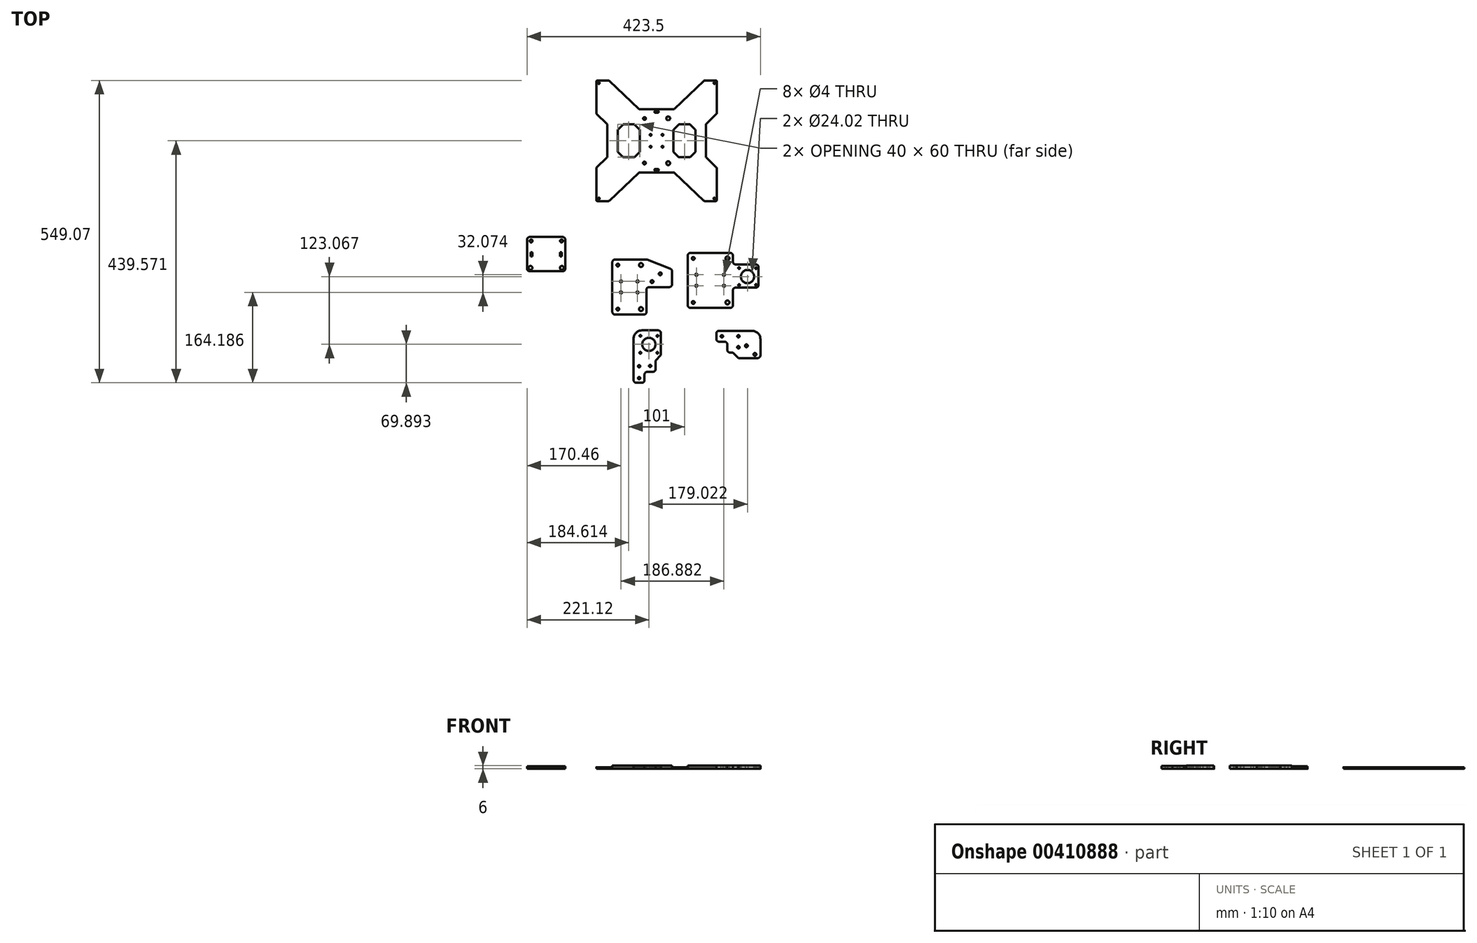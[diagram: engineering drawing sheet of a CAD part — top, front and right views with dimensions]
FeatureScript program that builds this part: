
annotation { "Feature Type Name" : "Feature", "Feature Type Description" : "" }
export const myFeature = defineFeature(function(context is Context, id is Id, definition is map)
    precondition{}
    {
        {
            var Q0;
            Q0=qCreatedBy(makeId("Top.planeOp"),FACE);
            var sketch = newSketch(context, id + "F0", { "sketchPlane" : qUnion([Q0])});
            skLineSegment(sketch, "E0", {"start": v(-27.76, 55) * mm, "end": v(-27.76, -40.26) * mm});
            skLineSegment(sketch, "E1", {"start": v(-27.76, -40.26) * mm, "end": v(-7.91, -40.26) * mm});
            skLineSegment(sketch, "E2", {"start": v(-7.91, -40.26) * mm, "end": v(-7.91, -20.34) * mm});
            skLineSegment(sketch, "E3", {"start": v(-7.91, -20.34) * mm, "end": v(12.1, -20.34) * mm});
            skLineSegment(sketch, "E4", {"start": v(12.1, -20.34) * mm, "end": v(12.1, 0) * mm});
            skLineSegment(sketch, "E5", {"start": v(12.1, 0) * mm, "end": v(21.88, 0) * mm});
            skLineSegment(sketch, "E6", {"start": v(21.88, 0) * mm, "end": v(21.88, 55) * mm});
            skLineSegment(sketch, "E7", {"start": v(21.88, 55) * mm, "end": v(-27.76, 55) * mm});
            skCircle(sketch, "E8", {"center": v(0, 29.63) * mm, "radius": 12 * mm});
            skCircle(sketch, "E9", {"center": v(-15.34, 45.09) * mm, "radius": 1.51 * mm});
            skCircle(sketch, "E10", {"center": v(-17.64, -10.14) * mm, "radius": 2.01 * mm});
            skCircle(sketch, "E11", {"center": v(2.3, -9.57) * mm, "radius": 2.01 * mm});
            skCircle(sketch, "E12", {"center": v(-17.64, -31.7) * mm, "radius": 2.01 * mm});
            skCircle(sketch, "E13.1.0", {"center": v(-15.45, 14.29) * mm, "radius": 1.51 * mm});
            skCircle(sketch, "E13.2.0", {"center": v(15.34, 14.18) * mm, "radius": 1.51 * mm});
            skCircle(sketch, "E13.3.0", {"center": v(15.45, 44.98) * mm, "radius": 1.51 * mm});
            skSolve(sketch);
        }
        {
            var Q0;
            Q0=makeQuery(id+"F0.imprint","IMPRINT",FACE,{"disambiguationData":[TD([[makeQuery(id+"F0.imprint","IMPRINT",EDGE,{"derivedFrom":sQuery(id+"F0.wireOp",EDGE,"E0")}),1.0]])]});
            extrude(context, id + "F1", {"entities" : qUnion([Q0]), "depth" : 5 * mm});
        }
        {
            var Q0;
            Q0=makeQuery(id+"F1.opExtrude","SWEPT_EDGE",EDGE,{"disambiguationData":[OSD([sQuery(id+"F0.wireOp",EDGE,"E0"),sQuery(id+"F0.wireOp",EDGE,"E7")])]});
            fillet(context, id + "F2", {"entities" : qUnion([Q0]), "radius" : 15 * mm, "tangentPropagation" : true, "allowEdgeOverflow" : false});
        }
        {
            var Q0;
            Q0=makeQuery(id+"F1.opExtrude","SWEPT_EDGE",EDGE,{"disambiguationData":[OSD([sQuery(id+"F0.wireOp",EDGE,"E6"),sQuery(id+"F0.wireOp",EDGE,"E7")])]});
            var Q1;
            Q1=makeQuery(id+"F1.opExtrude","SWEPT_EDGE",EDGE,{"disambiguationData":[OSD([sQuery(id+"F0.wireOp",EDGE,"E2"),sQuery(id+"F0.wireOp",EDGE,"E3")])]});
            var Q2;
            Q2=makeQuery(id+"F1.opExtrude","SWEPT_EDGE",EDGE,{"disambiguationData":[OSD([sQuery(id+"F0.wireOp",EDGE,"E1"),sQuery(id+"F0.wireOp",EDGE,"E2")])]});
            var Q3;
            Q3=makeQuery(id+"F1.opExtrude","SWEPT_EDGE",EDGE,{"disambiguationData":[OSD([sQuery(id+"F0.wireOp",EDGE,"E0"),sQuery(id+"F0.wireOp",EDGE,"E1")])]});
            var Q4;
            Q4=makeQuery(id+"F1.opExtrude","SWEPT_EDGE",EDGE,{"disambiguationData":[OSD([sQuery(id+"F0.wireOp",EDGE,"E3"),sQuery(id+"F0.wireOp",EDGE,"E4")])]});
            fillet(context, id + "F3", {"entities" : qUnion([Q0, Q1, Q2, Q3, Q4]), "radius" : 5 * mm, "tangentPropagation" : true, "allowEdgeOverflow" : false});
        }
        {
            var Q0;
            Q0=makeQuery(id+"F1.opExtrude","SWEPT_EDGE",EDGE,{"disambiguationData":[OSD([sQuery(id+"F0.wireOp",EDGE,"E5"),sQuery(id+"F0.wireOp",EDGE,"E6")])]});
            chamfer(context, id + "F4", {"entities" : qUnion([Q0]), "width" : 10 * mm, "tangentPropagation" : true});
        }
        {
            var Q0;
            Q0=qCreatedBy(makeId("Top.planeOp"),FACE);
            var sketch = newSketch(context, id + "F5", { "sketchPlane" : qUnion([Q0])});
            skLineSegment(sketch, "E14", {"start": v(70.52, 59.7) * mm, "end": v(152.52, 59.7) * mm});
            skLineSegment(sketch, "E15", {"start": v(152.52, 59.7) * mm, "end": v(152.52, 38.7) * mm});
            skLineSegment(sketch, "E16", {"start": v(152.52, 38.7) * mm, "end": v(199.02, 38.7) * mm});
            skLineSegment(sketch, "E17", {"start": v(199.02, 38.7) * mm, "end": v(199.02, -3.3) * mm});
            skLineSegment(sketch, "E18", {"start": v(199.02, -3.3) * mm, "end": v(152.52, -3.3) * mm});
            skLineSegment(sketch, "E19", {"start": v(152.52, -3.3) * mm, "end": v(152.52, -40.3) * mm});
            skLineSegment(sketch, "E20", {"start": v(152.52, -40.3) * mm, "end": v(70.52, -40.3) * mm});
            skLineSegment(sketch, "E21", {"start": v(70.52, -40.3) * mm, "end": v(70.52, 59.7) * mm});
            skCircle(sketch, "E22", {"center": v(179.02, 16.7) * mm, "radius": 12 * mm});
            skCircle(sketch, "E23", {"center": v(163.62, 32.1) * mm, "radius": 1.51 * mm});
            skCircle(sketch, "E24.1.0", {"center": v(163.62, 1.3) * mm, "radius": 1.51 * mm});
            skCircle(sketch, "E24.2.0", {"center": v(194.42, 1.3) * mm, "radius": 1.51 * mm});
            skCircle(sketch, "E24.3.0", {"center": v(194.42, 32.1) * mm, "radius": 1.51 * mm});
            skCircle(sketch, "E25", {"center": v(142.52, -30.3) * mm, "radius": 3.55 * mm});
            skLineSegment(sketch, "E26", {"start": v(111.52, 64.43) * mm, "end": v(111.52, -53.16) * mm, "construction": true});
            skLineSegment(sketch, "E27", {"start": v(70.52, 9.7) * mm, "end": v(217.27, 9.7) * mm, "construction": true});
            skCircle(sketch, "E28.MirrorC", {"center": v(142.52, 49.7) * mm, "radius": 3.55 * mm});
            skCircle(sketch, "E29", {"center": v(80.52, -30.3) * mm, "radius": 2.55 * mm});
            skCircle(sketch, "E30.MirrorC", {"center": v(80.52, 49.7) * mm, "radius": 2.55 * mm});
            skCircle(sketch, "E31", {"center": v(86.22, 0) * mm, "radius": 2 * mm});
            skCircle(sketch, "E32.0.1.0", {"center": v(86.22, 20) * mm, "radius": 2 * mm});
            skCircle(sketch, "E32.1.0.0", {"center": v(136.22, 0) * mm, "radius": 2 * mm});
            skCircle(sketch, "E32.1.1.0", {"center": v(136.22, 20) * mm, "radius": 2 * mm});
            skLineSegment(sketch, "E32.direction1", {"start": v(86.22, 0) * mm, "end": v(136.22, 0) * mm, "construction": true});
            skLineSegment(sketch, "E32.direction2", {"start": v(86.22, 0) * mm, "end": v(86.22, 20) * mm, "construction": true});
            skSolve(sketch);
        }
        {
            var Q0;
            Q0=makeQuery(id+"F5.imprint","IMPRINT",FACE,{"disambiguationData":[TD([[makeQuery(id+"F5.imprint","IMPRINT",EDGE,{"derivedFrom":sQuery(id+"F5.wireOp",EDGE,"E14")}),-1.0]])]});
            extrude(context, id + "F6", {"entities" : qUnion([Q0]), "depth" : 6 * mm});
        }
        {
            var Q0;
            Q0=makeQuery(id+"F6.opExtrude","SWEPT_EDGE",EDGE,{"disambiguationData":[OSD([sQuery(id+"F5.wireOp",EDGE,"E20"),sQuery(id+"F5.wireOp",EDGE,"E21")])]});
            var Q1;
            Q1=makeQuery(id+"F6.opExtrude","SWEPT_EDGE",EDGE,{"disambiguationData":[OSD([sQuery(id+"F5.wireOp",EDGE,"E19"),sQuery(id+"F5.wireOp",EDGE,"E20")])]});
            var Q2;
            Q2=makeQuery(id+"F6.opExtrude","SWEPT_EDGE",EDGE,{"disambiguationData":[OSD([sQuery(id+"F5.wireOp",EDGE,"E17"),sQuery(id+"F5.wireOp",EDGE,"E18")])]});
            var Q3;
            Q3=makeQuery(id+"F6.opExtrude","SWEPT_EDGE",EDGE,{"disambiguationData":[OSD([sQuery(id+"F5.wireOp",EDGE,"E18"),sQuery(id+"F5.wireOp",EDGE,"E19")])]});
            var Q4;
            Q4=makeQuery(id+"F6.opExtrude","SWEPT_EDGE",EDGE,{"disambiguationData":[OSD([sQuery(id+"F5.wireOp",EDGE,"E14"),sQuery(id+"F5.wireOp",EDGE,"E21")])]});
            var Q5;
            Q5=makeQuery(id+"F6.opExtrude","SWEPT_EDGE",EDGE,{"disambiguationData":[OSD([sQuery(id+"F5.wireOp",EDGE,"E14"),sQuery(id+"F5.wireOp",EDGE,"E15")])]});
            var Q6;
            Q6=makeQuery(id+"F6.opExtrude","SWEPT_EDGE",EDGE,{"disambiguationData":[OSD([sQuery(id+"F5.wireOp",EDGE,"E15"),sQuery(id+"F5.wireOp",EDGE,"E16")])]});
            var Q7;
            Q7=makeQuery(id+"F6.opExtrude","SWEPT_EDGE",EDGE,{"disambiguationData":[OSD([sQuery(id+"F5.wireOp",EDGE,"E16"),sQuery(id+"F5.wireOp",EDGE,"E17")])]});
            fillet(context, id + "F7", {"entities" : qUnion([Q0, Q1, Q2, Q3, Q4, Q5, Q6, Q7]), "radius" : 5 * mm, "tangentPropagation" : true, "allowEdgeOverflow" : false});
        }
        {
            var Q0;
            Q0=makeQuery(id+"F1.opExtrude","SWEPT_BODY",BODY,{"disambiguationData":[OSD([sQuery(id+"F0.wireOp",EDGE,"E0"),sQuery(id+"F0.wireOp",EDGE,"E1"),sQuery(id+"F0.wireOp",EDGE,"E2"),sQuery(id+"F0.wireOp",EDGE,"E3"),sQuery(id+"F0.wireOp",EDGE,"E4"),sQuery(id+"F0.wireOp",EDGE,"E5"),sQuery(id+"F0.wireOp",EDGE,"E6"),sQuery(id+"F0.wireOp",EDGE,"E7"),sQuery(id+"F0.wireOp",EDGE,"E8"),sQuery(id+"F0.wireOp",EDGE,"E9"),sQuery(id+"F0.wireOp",EDGE,"E10"),sQuery(id+"F0.wireOp",EDGE,"E11"),sQuery(id+"F0.wireOp",EDGE,"E12"),sQuery(id+"F0.wireOp",EDGE,"E13.1.0"),sQuery(id+"F0.wireOp",EDGE,"E13.2.0"),sQuery(id+"F0.wireOp",EDGE,"E13.3.0")])]});
            transform(context, id + "F8", {"entities" : qUnion([Q0]), "transformType" : TransformType.TRANSLATION_3D, "dx" : 0 * mm, "dy" : -136 * mm, "dz" : 0 * mm, "makeCopy" : false});
        }
        {
            var Q0;
            Q0=qCreatedBy(makeId("Top.planeOp"),FACE);
            var sketch = newSketch(context, id + "F9", { "sketchPlane" : qUnion([Q0])});
            skLineSegment(sketch, "E33", {"start": v(-66.36, 47.63) * mm, "end": v(-4.36, 47.63) * mm});
            skLineSegment(sketch, "E34", {"start": v(-4.36, 47.8) * mm, "end": v(-4.36, 47.63) * mm});
            skLineSegment(sketch, "E35", {"start": v(42.14, 29.63) * mm, "end": v(42.14, -2.37) * mm});
            skLineSegment(sketch, "E36", {"start": v(42.14, -2.37) * mm, "end": v(-4.36, -2.37) * mm});
            skLineSegment(sketch, "E37", {"start": v(-4.36, -2.37) * mm, "end": v(-4.36, -52.37) * mm});
            skLineSegment(sketch, "E38", {"start": v(-4.36, -52.37) * mm, "end": v(-66.36, -52.37) * mm});
            skLineSegment(sketch, "E39", {"start": v(-66.36, -52.37) * mm, "end": v(-66.36, 47.63) * mm});
            skCircle(sketch, "E40", {"center": v(-14.36, -42.37) * mm, "radius": 3.55 * mm});
            skLineSegment(sketch, "E41", {"start": v(-35.36, 52.36) * mm, "end": v(-35.36, -65.24) * mm, "construction": true});
            skLineSegment(sketch, "E42", {"start": v(-66.36, -2.37) * mm, "end": v(80.08, -2.37) * mm, "construction": true});
            skCircle(sketch, "E43.MirrorC", {"center": v(-14.36, 37.63) * mm, "radius": 3.55 * mm});
            skCircle(sketch, "E44", {"center": v(-56.36, -42.37) * mm, "radius": 2.55 * mm});
            skCircle(sketch, "E45.MirrorC", {"center": v(-56.36, 37.63) * mm, "radius": 2.55 * mm});
            skCircle(sketch, "E46", {"center": v(-50.66, -12.07) * mm, "radius": 2 * mm});
            skCircle(sketch, "E47.0.1.0", {"center": v(-50.66, 7.93) * mm, "radius": 2 * mm});
            skCircle(sketch, "E47.1.0.0", {"center": v(-20.66, -12.07) * mm, "radius": 2 * mm});
            skCircle(sketch, "E47.1.1.0", {"center": v(-20.66, 7.93) * mm, "radius": 2 * mm});
            skLineSegment(sketch, "E47.direction1", {"start": v(-50.66, -12.07) * mm, "end": v(-20.66, -12.07) * mm, "construction": true});
            skLineSegment(sketch, "E47.direction2", {"start": v(-50.66, -12.07) * mm, "end": v(-50.66, 7.93) * mm, "construction": true});
            skLineSegment(sketch, "E48", {"start": v(-4.36, 47.8) * mm, "end": v(42.14, 29.63) * mm});
            skLineSegment(sketch, "E49", {"start": v(-4.36, -2.37) * mm, "end": v(-4.36, 47.8) * mm, "construction": true});
            skCircle(sketch, "E50", {"center": v(5.64, 7.63) * mm, "radius": 2.6 * mm});
            skCircle(sketch, "E51", {"center": v(20.64, 21.63) * mm, "radius": 2.6 * mm});
            skSolve(sketch);
        }
        {
            var Q0;
            Q0=makeQuery(id+"F9.imprint","IMPRINT",FACE,{"disambiguationData":[TD([[makeQuery(id+"F9.imprint","IMPRINT",EDGE,{"derivedFrom":sQuery(id+"F9.wireOp",EDGE,"E33")}),-1.0]])]});
            extrude(context, id + "F10", {"entities" : qUnion([Q0]), "depth" : 6 * mm});
        }
        {
            var Q0;
            Q0=makeQuery(id+"F10.opExtrude","SWEPT_EDGE",EDGE,{"disambiguationData":[OSD([sQuery(id+"F9.wireOp",EDGE,"E34"),sQuery(id+"F9.wireOp",EDGE,"E48")])]});
            var Q1;
            Q1=makeQuery(id+"F10.opExtrude","SWEPT_EDGE",EDGE,{"disambiguationData":[OSD([sQuery(id+"F9.wireOp",EDGE,"E35"),sQuery(id+"F9.wireOp",EDGE,"E48")])]});
            var Q2;
            Q2=makeQuery(id+"F10.opExtrude","SWEPT_EDGE",EDGE,{"disambiguationData":[OSD([sQuery(id+"F9.wireOp",EDGE,"E35"),sQuery(id+"F9.wireOp",EDGE,"E36")])]});
            var Q3;
            Q3=makeQuery(id+"F10.opExtrude","SWEPT_EDGE",EDGE,{"disambiguationData":[OSD([sQuery(id+"F9.wireOp",EDGE,"E36"),sQuery(id+"F9.wireOp",EDGE,"E37")])]});
            var Q4;
            Q4=makeQuery(id+"F10.opExtrude","SWEPT_EDGE",EDGE,{"disambiguationData":[OSD([sQuery(id+"F9.wireOp",EDGE,"E37"),sQuery(id+"F9.wireOp",EDGE,"E38")])]});
            var Q5;
            Q5=makeQuery(id+"F10.opExtrude","SWEPT_EDGE",EDGE,{"disambiguationData":[OSD([sQuery(id+"F9.wireOp",EDGE,"E38"),sQuery(id+"F9.wireOp",EDGE,"E39")])]});
            var Q6;
            Q6=makeQuery(id+"F10.opExtrude","SWEPT_EDGE",EDGE,{"disambiguationData":[OSD([sQuery(id+"F9.wireOp",EDGE,"E33"),sQuery(id+"F9.wireOp",EDGE,"E39")])]});
            fillet(context, id + "F11", {"entities" : qUnion([Q0, Q1, Q2, Q3, Q4, Q5, Q6]), "radius" : 5 * mm, "tangentPropagation" : true, "allowEdgeOverflow" : false});
        }
        {
            var Q0;
            Q0=qCreatedBy(makeId("Top.planeOp"),FACE);
            var sketch = newSketch(context, id + "F12", { "sketchPlane" : qUnion([Q0])});
            skLineSegment(sketch, "E52", {"start": v(202.38, -81.82) * mm, "end": v(122.38, -81.82) * mm});
            skLineSegment(sketch, "E53", {"start": v(122.38, -81.82) * mm, "end": v(122.38, -101.56) * mm});
            skLineSegment(sketch, "E54", {"start": v(142.38, -101.56) * mm, "end": v(122.38, -101.56) * mm});
            skLineSegment(sketch, "E55", {"start": v(142.38, -101.56) * mm, "end": v(142.38, -121.39) * mm});
            skLineSegment(sketch, "E56", {"start": v(162.45, -121.39) * mm, "end": v(142.38, -121.39) * mm});
            skLineSegment(sketch, "E57", {"start": v(162.45, -121.39) * mm, "end": v(162.45, -131.39) * mm});
            skLineSegment(sketch, "E58", {"start": v(162.45, -131.39) * mm, "end": v(202.38, -131.39) * mm});
            skLineSegment(sketch, "E59", {"start": v(202.38, -131.39) * mm, "end": v(202.38, -81.82) * mm});
            skCircle(sketch, "E60", {"center": v(132.43, -91.69) * mm, "radius": 2.12 * mm});
            skPoint(sketch, "E60.centerSnap0", {"position": v(122.38, -91.69) * mm});
            skCircle(sketch, "E61", {"center": v(162.43, -91.69) * mm, "radius": 2.12 * mm});
            skCircle(sketch, "E62", {"center": v(162.45, -111.69) * mm, "radius": 2.17 * mm});
            skLineSegment(sketch, "E63", {"start": v(162.43, -79.74) * mm, "end": v(162.45, -129.84) * mm, "construction": true});
            skCircle(sketch, "E64", {"center": v(176.96, -109) * mm, "radius": 2.58 * mm});
            skCircle(sketch, "E65", {"center": v(192.38, -124.64) * mm, "radius": 2.58 * mm});
            skSolve(sketch);
        }
        {
            var Q0;
            Q0=makeQuery(id+"F12.imprint","IMPRINT",FACE,{"disambiguationData":[TD([[makeQuery(id+"F12.imprint","IMPRINT",EDGE,{"derivedFrom":sQuery(id+"F12.wireOp",EDGE,"E52")}),1.0]])]});
            extrude(context, id + "F13", {"entities" : qUnion([Q0]), "depth" : 6 * mm});
        }
        {
            var Q0;
            Q0=makeQuery(id+"F13.opExtrude","SWEPT_EDGE",EDGE,{"disambiguationData":[OSD([sQuery(id+"F12.wireOp",EDGE,"E52"),sQuery(id+"F12.wireOp",EDGE,"E53")])]});
            var Q1;
            Q1=makeQuery(id+"F13.opExtrude","SWEPT_EDGE",EDGE,{"disambiguationData":[OSD([sQuery(id+"F12.wireOp",EDGE,"E53"),sQuery(id+"F12.wireOp",EDGE,"E54")])]});
            var Q2;
            Q2=makeQuery(id+"F13.opExtrude","SWEPT_EDGE",EDGE,{"disambiguationData":[OSD([sQuery(id+"F12.wireOp",EDGE,"E54"),sQuery(id+"F12.wireOp",EDGE,"E55")])]});
            var Q3;
            Q3=makeQuery(id+"F13.opExtrude","SWEPT_EDGE",EDGE,{"disambiguationData":[OSD([sQuery(id+"F12.wireOp",EDGE,"E55"),sQuery(id+"F12.wireOp",EDGE,"E56")])]});
            var Q4;
            Q4=makeQuery(id+"F13.opExtrude","SWEPT_EDGE",EDGE,{"disambiguationData":[OSD([sQuery(id+"F12.wireOp",EDGE,"E58"),sQuery(id+"F12.wireOp",EDGE,"E59")])]});
            fillet(context, id + "F14", {"entities" : qUnion([Q0, Q1, Q2, Q3, Q4]), "radius" : 5 * mm, "tangentPropagation" : true, "allowEdgeOverflow" : false});
        }
        {
            var Q0;
            Q0=makeQuery(id+"F13.opExtrude","SWEPT_EDGE",EDGE,{"disambiguationData":[OSD([sQuery(id+"F12.wireOp",EDGE,"E56"),sQuery(id+"F12.wireOp",EDGE,"E57")])]});
            chamfer(context, id + "F15", {"entities" : qUnion([Q0]), "width" : 10 * mm, "tangentPropagation" : true});
        }
        {
            var Q0;
            Q0=makeQuery(id+"F13.opExtrude","SWEPT_EDGE",EDGE,{"disambiguationData":[OSD([sQuery(id+"F12.wireOp",EDGE,"E52"),sQuery(id+"F12.wireOp",EDGE,"E59")])]});
            fillet(context, id + "F16", {"entities" : qUnion([Q0]), "radius" : 15 * mm, "tangentPropagation" : true, "allowEdgeOverflow" : false});
        }
        {
            var Q0;
            Q0=qCreatedBy(makeId("Top.planeOp"),FACE);
            var sketch = newSketch(context, id + "F17", { "sketchPlane" : qUnion([Q0])});
            skLineSegment(sketch, "E66.bottom", {"start": v(-95.5, 372.81) * mm, "end": v(-72.5, 372.81) * mm});
            skLineSegment(sketch, "E66.top", {"start": v(-95.5, 153.81) * mm, "end": v(-72.5, 153.81) * mm});
            skLineSegment(sketch, "E66.left", {"start": v(-95.5, 372.81) * mm, "end": v(-95.5, 312.81) * mm});
            skLineSegment(sketch, "E66.right", {"start": v(123.5, 372.81) * mm, "end": v(123.5, 312.81) * mm});
            skPoint(sketch, "E67", {"position": v(-75.5, 263.31) * mm});
            skPoint(sketch, "E68", {"position": v(-95.5, 213.81) * mm});
            skLineSegment(sketch, "E69", {"start": v(-75.5, 263.31) * mm, "end": v(-75.5, 233.31) * mm});
            skLineSegment(sketch, "E70", {"start": v(-95.5, 213.81) * mm, "end": v(-75.5, 233.31) * mm});
            skPoint(sketch, "E71", {"position": v(-56.5, 263.31) * mm});
            skPoint(sketch, "E72", {"position": v(-16.5, 263.31) * mm});
            skPoint(sketch, "E73", {"position": v(-36.5, 263.31) * mm});
            skPoint(sketch, "E74", {"position": v(-36.5, 233.31) * mm});
            skLineSegment(sketch, "E75", {"start": v(-36.5, 233.31) * mm, "end": v(-26.5, 233.31) * mm});
            skLineSegment(sketch, "E76", {"start": v(-26.5, 233.31) * mm, "end": v(-36.5, 233.31) * mm});
            skLineSegment(sketch, "E77", {"start": v(-46.5, 233.31) * mm, "end": v(-36.5, 233.31) * mm});
            skLineSegment(sketch, "E78", {"start": v(-56.5, 263.31) * mm, "end": v(-56.5, 243.31) * mm});
            skLineSegment(sketch, "E79", {"start": v(-56.5, 243.31) * mm, "end": v(-46.5, 233.31) * mm});
            skLineSegment(sketch, "E80", {"start": v(-16.5, 263.31) * mm, "end": v(-16.5, 243.31) * mm});
            skLineSegment(sketch, "E81", {"start": v(-26.5, 233.31) * mm, "end": v(-16.5, 243.31) * mm});
            skPoint(sketch, "E82", {"position": v(-95.5, 205.81) * mm});
            skPoint(sketch, "E83", {"position": v(14, 205.81) * mm});
            skLineSegment(sketch, "E84", {"start": v(14, 205.81) * mm, "end": v(-18, 205.81) * mm});
            skPoint(sketch, "E85", {"position": v(-72.5, 153.81) * mm});
            skLineSegment(sketch, "E86", {"start": v(-72.5, 153.81) * mm, "end": v(-18, 205.81) * mm});
            skLineSegment(sketch, "E87.MirrorCS", {"start": v(44.5, 263.31) * mm, "end": v(44.5, 243.31) * mm});
            skLineSegment(sketch, "E88.MirrorCS", {"start": v(54.5, 233.31) * mm, "end": v(44.5, 243.31) * mm});
            skLineSegment(sketch, "E89.MirrorCS", {"start": v(54.5, 233.31) * mm, "end": v(64.5, 233.31) * mm});
            skLineSegment(sketch, "E90.MirrorCS", {"start": v(74.5, 233.31) * mm, "end": v(64.5, 233.31) * mm});
            skLineSegment(sketch, "E91.MirrorCS", {"start": v(84.5, 243.31) * mm, "end": v(74.5, 233.31) * mm});
            skLineSegment(sketch, "E92.MirrorCS", {"start": v(84.5, 263.31) * mm, "end": v(84.5, 243.31) * mm});
            skLineSegment(sketch, "E93.MirrorCS", {"start": v(103.5, 263.31) * mm, "end": v(103.5, 233.31) * mm});
            skLineSegment(sketch, "E94.MirrorCS", {"start": v(123.5, 213.81) * mm, "end": v(103.5, 233.31) * mm});
            skLineSegment(sketch, "E95.MirrorCS", {"start": v(100.5, 153.81) * mm, "end": v(46, 205.81) * mm});
            skLineSegment(sketch, "E96.MirrorCS", {"start": v(14, 205.81) * mm, "end": v(46, 205.81) * mm});
            skLineSegment(sketch, "E97.MirrorCS", {"start": v(-75.5, 263.31) * mm, "end": v(-75.5, 293.31) * mm});
            skLineSegment(sketch, "E98.MirrorCS", {"start": v(-95.5, 312.81) * mm, "end": v(-75.5, 293.31) * mm});
            skLineSegment(sketch, "E99.MirrorCS", {"start": v(-56.5, 263.31) * mm, "end": v(-56.5, 283.31) * mm});
            skLineSegment(sketch, "E100.MirrorCS", {"start": v(-56.5, 283.31) * mm, "end": v(-46.5, 293.31) * mm});
            skLineSegment(sketch, "E101.MirrorCS", {"start": v(-46.5, 293.31) * mm, "end": v(-36.5, 293.31) * mm});
            skLineSegment(sketch, "E102.MirrorCS", {"start": v(-26.5, 293.31) * mm, "end": v(-36.5, 293.31) * mm});
            skLineSegment(sketch, "E103.MirrorCS", {"start": v(-26.5, 293.31) * mm, "end": v(-16.5, 283.31) * mm});
            skLineSegment(sketch, "E104.MirrorCS", {"start": v(-16.5, 263.31) * mm, "end": v(-16.5, 283.31) * mm});
            skLineSegment(sketch, "E105.MirrorCS", {"start": v(44.5, 263.31) * mm, "end": v(44.5, 283.31) * mm});
            skLineSegment(sketch, "E106.MirrorCS", {"start": v(54.5, 293.31) * mm, "end": v(44.5, 283.31) * mm});
            skLineSegment(sketch, "E107.MirrorCS", {"start": v(54.5, 293.31) * mm, "end": v(64.5, 293.31) * mm});
            skLineSegment(sketch, "E108.MirrorCS", {"start": v(74.5, 293.31) * mm, "end": v(64.5, 293.31) * mm});
            skLineSegment(sketch, "E109.MirrorCS", {"start": v(84.5, 283.31) * mm, "end": v(74.5, 293.31) * mm});
            skLineSegment(sketch, "E110.MirrorCS", {"start": v(84.5, 263.31) * mm, "end": v(84.5, 283.31) * mm});
            skLineSegment(sketch, "E111.MirrorCS", {"start": v(103.5, 263.31) * mm, "end": v(103.5, 293.31) * mm});
            skLineSegment(sketch, "E112.MirrorCS", {"start": v(123.5, 312.81) * mm, "end": v(103.5, 293.31) * mm});
            skLineSegment(sketch, "E113.MirrorCS", {"start": v(14, 320.81) * mm, "end": v(-18, 320.81) * mm});
            skLineSegment(sketch, "E114.MirrorCS", {"start": v(-72.5, 372.81) * mm, "end": v(-18, 320.81) * mm});
            skLineSegment(sketch, "E115.MirrorCS", {"start": v(14, 320.81) * mm, "end": v(46, 320.81) * mm});
            skLineSegment(sketch, "E116.MirrorCS", {"start": v(100.5, 372.81) * mm, "end": v(46, 320.81) * mm});
            skLineSegment(sketch, "E117.trimOffspring", {"start": v(-95.5, 213.81) * mm, "end": v(-95.5, 153.81) * mm});
            skLineSegment(sketch, "E118.trimOffspring", {"start": v(123.5, 213.81) * mm, "end": v(123.5, 153.81) * mm});
            skLineSegment(sketch, "E119.trimOffspring", {"start": v(100.5, 153.81) * mm, "end": v(123.5, 153.81) * mm});
            skLineSegment(sketch, "E120.trimOffspring", {"start": v(100.5, 372.81) * mm, "end": v(123.5, 372.81) * mm});
            skCircle(sketch, "E121", {"center": v(-90.84, 368.14) * mm, "radius": 1.6 * mm});
            skCircle(sketch, "E122", {"center": v(3.2, 274.1) * mm, "radius": 1.6 * mm});
            skCircle(sketch, "E123.MirrorC", {"center": v(118.83, 158.48) * mm, "radius": 1.6 * mm});
            skCircle(sketch, "E124.MirrorC", {"center": v(24.78, 252.52) * mm, "radius": 1.6 * mm});
            skCircle(sketch, "E125.MirrorC", {"center": v(24.78, 274.1) * mm, "radius": 1.6 * mm});
            skCircle(sketch, "E126.MirrorC", {"center": v(3.2, 252.52) * mm, "radius": 1.6 * mm});
            skCircle(sketch, "E127.MirrorC", {"center": v(118.83, 368.14) * mm, "radius": 1.6 * mm});
            skCircle(sketch, "E128.MirrorC", {"center": v(-90.84, 158.48) * mm, "radius": 1.6 * mm});
            skLineSegment(sketch, "E129.bottom", {"start": v(10, 212.31) * mm, "end": v(18, 212.31) * mm});
            skLineSegment(sketch, "E129.top", {"start": v(10, 208.81) * mm, "end": v(18, 208.81) * mm});
            skLineSegment(sketch, "E129.left", {"start": v(10, 212.31) * mm, "end": v(10, 208.81) * mm});
            skLineSegment(sketch, "E129.right", {"start": v(18, 212.31) * mm, "end": v(18, 208.81) * mm});
            skPoint(sketch, "E130", {"position": v(14, 212.31) * mm});
            skLineSegment(sketch, "E131.MirrorCS", {"start": v(10, 314.31) * mm, "end": v(18, 314.31) * mm});
            skLineSegment(sketch, "E132.MirrorCS", {"start": v(10, 314.31) * mm, "end": v(10, 317.81) * mm});
            skLineSegment(sketch, "E133.MirrorCS", {"start": v(10, 317.81) * mm, "end": v(18, 317.81) * mm});
            skLineSegment(sketch, "E134.MirrorCS", {"start": v(18, 314.31) * mm, "end": v(18, 317.81) * mm});
            skCircle(sketch, "E135", {"center": v(35, 222.56) * mm, "radius": 3.5 * mm});
            skCircle(sketch, "E136", {"center": v(-8, 222.86) * mm, "radius": 2.5 * mm});
            skCircle(sketch, "E137.MirrorC", {"center": v(-8, 303.76) * mm, "radius": 2.5 * mm});
            skCircle(sketch, "E138.MirrorC", {"center": v(35, 304.06) * mm, "radius": 3.5 * mm});
            skSolve(sketch);
        }
        {
            var Q0;
            Q0=makeQuery(id+"F17.imprint","IMPRINT",FACE,{"disambiguationData":[TD([[makeQuery(id+"F17.imprint","IMPRINT",EDGE,{"derivedFrom":sQuery(id+"F17.wireOp",EDGE,"E66.bottom")}),-1.0]])]});
            extrude(context, id + "F18", {"entities" : qUnion([Q0]), "depth" : 3 * mm});
        }
        {
            var Q0;
            Q0=makeQuery(id+"F18.opExtrude","SWEPT_EDGE",EDGE,{"disambiguationData":[OSD([sQuery(id+"F17.wireOp",EDGE,"E84"),sQuery(id+"F17.wireOp",EDGE,"E86")])]});
            var Q1;
            Q1=makeQuery(id+"F18.opExtrude","SWEPT_EDGE",EDGE,{"disambiguationData":[OSD([sQuery(id+"F17.wireOp",EDGE,"E95.MirrorCS"),sQuery(id+"F17.wireOp",EDGE,"E96.MirrorCS")])]});
            var Q2;
            Q2=makeQuery(id+"F18.opExtrude","SWEPT_EDGE",EDGE,{"disambiguationData":[OSD([sQuery(id+"F17.wireOp",EDGE,"E95.MirrorCS"),sQuery(id+"F17.wireOp",EDGE,"E119.trimOffspring")])]});
            var Q3;
            Q3=makeQuery(id+"F18.opExtrude","SWEPT_EDGE",EDGE,{"disambiguationData":[OSD([sQuery(id+"F17.wireOp",EDGE,"E118.trimOffspring"),sQuery(id+"F17.wireOp",EDGE,"E119.trimOffspring")])]});
            var Q4;
            Q4=makeQuery(id+"F18.opExtrude","SWEPT_EDGE",EDGE,{"disambiguationData":[OSD([sQuery(id+"F17.wireOp",EDGE,"E129.bottom"),sQuery(id+"F17.wireOp",EDGE,"E129.left")])]});
            var Q5;
            Q5=makeQuery(id+"F18.opExtrude","SWEPT_EDGE",EDGE,{"disambiguationData":[OSD([sQuery(id+"F17.wireOp",EDGE,"E129.bottom"),sQuery(id+"F17.wireOp",EDGE,"E129.right")])]});
            var Q6;
            Q6=makeQuery(id+"F18.opExtrude","SWEPT_EDGE",EDGE,{"disambiguationData":[OSD([sQuery(id+"F17.wireOp",EDGE,"E129.top"),sQuery(id+"F17.wireOp",EDGE,"E129.right")])]});
            var Q7;
            Q7=makeQuery(id+"F18.opExtrude","SWEPT_EDGE",EDGE,{"disambiguationData":[OSD([sQuery(id+"F17.wireOp",EDGE,"E129.top"),sQuery(id+"F17.wireOp",EDGE,"E129.left")])]});
            var Q8;
            Q8=makeQuery(id+"F18.opExtrude","SWEPT_EDGE",EDGE,{"disambiguationData":[OSD([sQuery(id+"F17.wireOp",EDGE,"E76"),sQuery(id+"F17.wireOp",EDGE,"E81")])]});
            var Q9;
            Q9=makeQuery(id+"F18.opExtrude","SWEPT_EDGE",EDGE,{"disambiguationData":[OSD([sQuery(id+"F17.wireOp",EDGE,"E80"),sQuery(id+"F17.wireOp",EDGE,"E81")])]});
            var Q10;
            Q10=makeQuery(id+"F18.opExtrude","SWEPT_EDGE",EDGE,{"disambiguationData":[OSD([sQuery(id+"F17.wireOp",EDGE,"E90.MirrorCS"),sQuery(id+"F17.wireOp",EDGE,"E91.MirrorCS")])]});
            var Q11;
            Q11=makeQuery(id+"F18.opExtrude","SWEPT_EDGE",EDGE,{"disambiguationData":[OSD([sQuery(id+"F17.wireOp",EDGE,"E66.bottom"),sQuery(id+"F17.wireOp",EDGE,"E66.left")])]});
            var Q12;
            Q12=makeQuery(id+"F18.opExtrude","SWEPT_EDGE",EDGE,{"disambiguationData":[OSD([sQuery(id+"F17.wireOp",EDGE,"E70"),sQuery(id+"F17.wireOp",EDGE,"E117.trimOffspring")])]});
            var Q13;
            Q13=makeQuery(id+"F18.opExtrude","SWEPT_EDGE",EDGE,{"disambiguationData":[OSD([sQuery(id+"F17.wireOp",EDGE,"E69"),sQuery(id+"F17.wireOp",EDGE,"E70")])]});
            var Q14;
            Q14=makeQuery(id+"F18.opExtrude","SWEPT_EDGE",EDGE,{"disambiguationData":[OSD([sQuery(id+"F17.wireOp",EDGE,"E66.left"),sQuery(id+"F17.wireOp",EDGE,"E98.MirrorCS")])]});
            var Q15;
            Q15=makeQuery(id+"F18.opExtrude","SWEPT_EDGE",EDGE,{"disambiguationData":[OSD([sQuery(id+"F17.wireOp",EDGE,"E116.MirrorCS"),sQuery(id+"F17.wireOp",EDGE,"E120.trimOffspring")])]});
            var Q16;
            Q16=makeQuery(id+"F18.opExtrude","SWEPT_EDGE",EDGE,{"disambiguationData":[OSD([sQuery(id+"F17.wireOp",EDGE,"E66.right"),sQuery(id+"F17.wireOp",EDGE,"E120.trimOffspring")])]});
            var Q17;
            Q17=makeQuery(id+"F18.opExtrude","SWEPT_EDGE",EDGE,{"disambiguationData":[OSD([sQuery(id+"F17.wireOp",EDGE,"E66.bottom"),sQuery(id+"F17.wireOp",EDGE,"E114.MirrorCS")])]});
            var Q18;
            Q18=makeQuery(id+"F18.opExtrude","SWEPT_EDGE",EDGE,{"disambiguationData":[OSD([sQuery(id+"F17.wireOp",EDGE,"E88.MirrorCS"),sQuery(id+"F17.wireOp",EDGE,"E89.MirrorCS")])]});
            var Q19;
            Q19=makeQuery(id+"F18.opExtrude","SWEPT_EDGE",EDGE,{"disambiguationData":[OSD([sQuery(id+"F17.wireOp",EDGE,"E94.MirrorCS"),sQuery(id+"F17.wireOp",EDGE,"E118.trimOffspring")])]});
            var Q20;
            Q20=makeQuery(id+"F18.opExtrude","SWEPT_EDGE",EDGE,{"disambiguationData":[OSD([sQuery(id+"F17.wireOp",EDGE,"E93.MirrorCS"),sQuery(id+"F17.wireOp",EDGE,"E94.MirrorCS")])]});
            var Q21;
            Q21=makeQuery(id+"F18.opExtrude","SWEPT_EDGE",EDGE,{"disambiguationData":[OSD([sQuery(id+"F17.wireOp",EDGE,"E111.MirrorCS"),sQuery(id+"F17.wireOp",EDGE,"E112.MirrorCS")])]});
            var Q22;
            Q22=makeQuery(id+"F18.opExtrude","SWEPT_EDGE",EDGE,{"disambiguationData":[OSD([sQuery(id+"F17.wireOp",EDGE,"E66.right"),sQuery(id+"F17.wireOp",EDGE,"E112.MirrorCS")])]});
            var Q23;
            Q23=makeQuery(id+"F18.opExtrude","SWEPT_EDGE",EDGE,{"disambiguationData":[OSD([sQuery(id+"F17.wireOp",EDGE,"E105.MirrorCS"),sQuery(id+"F17.wireOp",EDGE,"E106.MirrorCS")])]});
            var Q24;
            Q24=makeQuery(id+"F18.opExtrude","SWEPT_EDGE",EDGE,{"disambiguationData":[OSD([sQuery(id+"F17.wireOp",EDGE,"E77"),sQuery(id+"F17.wireOp",EDGE,"E79")])]});
            var Q25;
            Q25=makeQuery(id+"F18.opExtrude","SWEPT_EDGE",EDGE,{"disambiguationData":[OSD([sQuery(id+"F17.wireOp",EDGE,"E78"),sQuery(id+"F17.wireOp",EDGE,"E79")])]});
            var Q26;
            Q26=makeQuery(id+"F18.opExtrude","SWEPT_EDGE",EDGE,{"disambiguationData":[OSD([sQuery(id+"F17.wireOp",EDGE,"E99.MirrorCS"),sQuery(id+"F17.wireOp",EDGE,"E100.MirrorCS")])]});
            var Q27;
            Q27=makeQuery(id+"F18.opExtrude","SWEPT_EDGE",EDGE,{"disambiguationData":[OSD([sQuery(id+"F17.wireOp",EDGE,"E113.MirrorCS"),sQuery(id+"F17.wireOp",EDGE,"E114.MirrorCS")])]});
            var Q28;
            Q28=makeQuery(id+"F18.opExtrude","SWEPT_EDGE",EDGE,{"disambiguationData":[OSD([sQuery(id+"F17.wireOp",EDGE,"E115.MirrorCS"),sQuery(id+"F17.wireOp",EDGE,"E116.MirrorCS")])]});
            var Q29;
            Q29=makeQuery(id+"F18.opExtrude","SWEPT_EDGE",EDGE,{"disambiguationData":[OSD([sQuery(id+"F17.wireOp",EDGE,"E91.MirrorCS"),sQuery(id+"F17.wireOp",EDGE,"E92.MirrorCS")])]});
            var Q30;
            Q30=makeQuery(id+"F18.opExtrude","SWEPT_EDGE",EDGE,{"disambiguationData":[OSD([sQuery(id+"F17.wireOp",EDGE,"E108.MirrorCS"),sQuery(id+"F17.wireOp",EDGE,"E109.MirrorCS")])]});
            var Q31;
            Q31=makeQuery(id+"F18.opExtrude","SWEPT_EDGE",EDGE,{"disambiguationData":[OSD([sQuery(id+"F17.wireOp",EDGE,"E106.MirrorCS"),sQuery(id+"F17.wireOp",EDGE,"E107.MirrorCS")])]});
            var Q32;
            Q32=makeQuery(id+"F18.opExtrude","SWEPT_EDGE",EDGE,{"disambiguationData":[OSD([sQuery(id+"F17.wireOp",EDGE,"E102.MirrorCS"),sQuery(id+"F17.wireOp",EDGE,"E103.MirrorCS")])]});
            var Q33;
            Q33=makeQuery(id+"F18.opExtrude","SWEPT_EDGE",EDGE,{"disambiguationData":[OSD([sQuery(id+"F17.wireOp",EDGE,"E100.MirrorCS"),sQuery(id+"F17.wireOp",EDGE,"E101.MirrorCS")])]});
            var Q34;
            Q34=makeQuery(id+"F18.opExtrude","SWEPT_EDGE",EDGE,{"disambiguationData":[OSD([sQuery(id+"F17.wireOp",EDGE,"E103.MirrorCS"),sQuery(id+"F17.wireOp",EDGE,"E104.MirrorCS")])]});
            var Q35;
            Q35=makeQuery(id+"F18.opExtrude","SWEPT_EDGE",EDGE,{"disambiguationData":[OSD([sQuery(id+"F17.wireOp",EDGE,"E109.MirrorCS"),sQuery(id+"F17.wireOp",EDGE,"E110.MirrorCS")])]});
            var Q36;
            Q36=makeQuery(id+"F18.opExtrude","SWEPT_EDGE",EDGE,{"disambiguationData":[OSD([sQuery(id+"F17.wireOp",EDGE,"E66.top"),sQuery(id+"F17.wireOp",EDGE,"E86")])]});
            var Q37;
            Q37=makeQuery(id+"F18.opExtrude","SWEPT_EDGE",EDGE,{"disambiguationData":[OSD([sQuery(id+"F17.wireOp",EDGE,"E66.top"),sQuery(id+"F17.wireOp",EDGE,"E117.trimOffspring")])]});
            var Q38;
            Q38=makeQuery(id+"F18.opExtrude","SWEPT_EDGE",EDGE,{"disambiguationData":[OSD([sQuery(id+"F17.wireOp",EDGE,"E97.MirrorCS"),sQuery(id+"F17.wireOp",EDGE,"E98.MirrorCS")])]});
            var Q39;
            Q39=makeQuery(id+"F18.opExtrude","SWEPT_EDGE",EDGE,{"disambiguationData":[OSD([sQuery(id+"F17.wireOp",EDGE,"E131.MirrorCS"),sQuery(id+"F17.wireOp",EDGE,"E134.MirrorCS")])]});
            var Q40;
            Q40=makeQuery(id+"F18.opExtrude","SWEPT_EDGE",EDGE,{"disambiguationData":[OSD([sQuery(id+"F17.wireOp",EDGE,"E133.MirrorCS"),sQuery(id+"F17.wireOp",EDGE,"E134.MirrorCS")])]});
            var Q41;
            Q41=makeQuery(id+"F18.opExtrude","SWEPT_EDGE",EDGE,{"disambiguationData":[OSD([sQuery(id+"F17.wireOp",EDGE,"E132.MirrorCS"),sQuery(id+"F17.wireOp",EDGE,"E133.MirrorCS")])]});
            var Q42;
            Q42=makeQuery(id+"F18.opExtrude","SWEPT_EDGE",EDGE,{"disambiguationData":[OSD([sQuery(id+"F17.wireOp",EDGE,"E131.MirrorCS"),sQuery(id+"F17.wireOp",EDGE,"E132.MirrorCS")])]});
            fillet(context, id + "F19", {"entities" : qUnion([Q0, Q1, Q2, Q3, Q4, Q5, Q6, Q7, Q8, Q9, Q10, Q11, Q12, Q13, Q14, Q15, Q16, Q17, Q18, Q19, Q20, Q21, Q22, Q23, Q24, Q25, Q26, Q27, Q28, Q29, Q30, Q31, Q32, Q33, Q34, Q35, Q36, Q37, Q38, Q39, Q40, Q41, Q42]), "radius" : 2 * mm, "tangentPropagation" : true, "allowEdgeOverflow" : false});
        }
        {
            var Q0;
            Q0=qCreatedBy(makeId("Top.planeOp"),FACE);
            var sketch = newSketch(context, id + "F20", { "sketchPlane" : qUnion([Q0])});
            skLineSegment(sketch, "E139.bottom", {"start": v(-221.12, 88.57) * mm, "end": v(-151.72, 88.57) * mm});
            skLineSegment(sketch, "E139.top", {"start": v(-221.12, 26.27) * mm, "end": v(-151.72, 26.27) * mm});
            skLineSegment(sketch, "E139.left", {"start": v(-221.12, 88.57) * mm, "end": v(-221.12, 26.27) * mm});
            skLineSegment(sketch, "E139.right", {"start": v(-151.72, 88.57) * mm, "end": v(-151.72, 26.27) * mm});
            skLineSegment(sketch, "E140.bottom", {"start": v(-204.58, 88.57) * mm, "end": v(-167.02, 88.57) * mm});
            skLineSegment(sketch, "E140.top", {"start": v(-204.58, 116.13) * mm, "end": v(-167.02, 116.13) * mm});
            skLineSegment(sketch, "E140.left", {"start": v(-204.58, 88.57) * mm, "end": v(-204.58, 116.13) * mm});
            skLineSegment(sketch, "E140.right", {"start": v(-167.02, 88.57) * mm, "end": v(-167.02, 116.13) * mm});
            skCircle(sketch, "E141", {"center": v(-214.92, 32.47) * mm, "radius": 3.5 * mm});
            skCircle(sketch, "E142", {"center": v(-157.92, 32.47) * mm, "radius": 3.5 * mm});
            skCircle(sketch, "E143", {"center": v(-213.72, 81.37) * mm, "radius": 2.55 * mm});
            skCircle(sketch, "E144", {"center": v(-158.52, 81.37) * mm, "radius": 2.55 * mm});
            skLineSegment(sketch, "E145.bottom", {"start": v(-214.82, 60.67) * mm, "end": v(-211.62, 60.67) * mm});
            skLineSegment(sketch, "E145.top", {"start": v(-214.82, 53.47) * mm, "end": v(-211.62, 53.47) * mm});
            skLineSegment(sketch, "E145.left", {"start": v(-214.82, 60.67) * mm, "end": v(-214.82, 53.47) * mm});
            skLineSegment(sketch, "E145.right", {"start": v(-211.62, 60.67) * mm, "end": v(-211.62, 53.47) * mm});
            skLineSegment(sketch, "E146.bottom", {"start": v(-161.22, 60.67) * mm, "end": v(-158.02, 60.67) * mm});
            skLineSegment(sketch, "E146.top", {"start": v(-161.22, 53.47) * mm, "end": v(-158.02, 53.47) * mm});
            skLineSegment(sketch, "E146.left", {"start": v(-161.22, 60.67) * mm, "end": v(-161.22, 53.47) * mm});
            skLineSegment(sketch, "E146.right", {"start": v(-158.02, 60.67) * mm, "end": v(-158.02, 53.47) * mm});
            skCircle(sketch, "E147", {"center": v(-185.8, 102.35) * mm, "radius": 6.1 * mm});
            skPoint(sketch, "E147.centerSnap0", {"position": v(-204.58, 102.35) * mm});
            skPoint(sketch, "E147.centerSnap1", {"position": v(-185.8, 116.13) * mm});
            skSolve(sketch);
        }
        {
            var Q0;
            Q0=makeQuery(id+"F20.imprint","IMPRINT",FACE,{"disambiguationData":[TD([[makeQuery(id+"F20.imprint","IMPRINT",EDGE,{"derivedFrom":sQuery(id+"F20.wireOp",EDGE,"E139.top")}),1.0]])]});
            var Q1;
            Q1=makeQuery(id+"F20.imprint","IMPRINT",FACE,{"disambiguationData":[TD([[makeQuery(id+"F20.imprint","IMPRINT",EDGE,{"derivedFrom":sQuery(id+"F20.wireOp",EDGE,"E140.bottom")}),1.0]])]});
            extrude(context, id + "F21", {"entities" : qUnion([Q0, Q1]), "depth" : 4.5 * mm});
        }
        {
            var Q0;
            Q0=makeQuery(id+"F21.opExtrude","SWEPT_EDGE",EDGE,{"disambiguationData":[OSD([sQuery(id+"F20.wireOp",EDGE,"E139.bottom"),sQuery(id+"F20.wireOp",EDGE,"E139.left")])]});
            var Q1;
            Q1=makeQuery(id+"F21.opExtrude","SWEPT_EDGE",EDGE,{"disambiguationData":[OSD([sQuery(id+"F20.wireOp",EDGE,"E139.bottom"),sQuery(id+"F20.wireOp",EDGE,"E140.bottom"),sQuery(id+"F20.wireOp",EDGE,"E140.left")])]});
            var Q2;
            Q2=makeQuery(id+"F21.opExtrude","SWEPT_EDGE",EDGE,{"disambiguationData":[OSD([sQuery(id+"F20.wireOp",EDGE,"E140.top"),sQuery(id+"F20.wireOp",EDGE,"E140.left")])]});
            var Q3;
            Q3=makeQuery(id+"F21.opExtrude","SWEPT_EDGE",EDGE,{"disambiguationData":[OSD([sQuery(id+"F20.wireOp",EDGE,"E139.top"),sQuery(id+"F20.wireOp",EDGE,"E139.right")])]});
            var Q4;
            Q4=makeQuery(id+"F21.opExtrude","SWEPT_EDGE",EDGE,{"disambiguationData":[OSD([sQuery(id+"F20.wireOp",EDGE,"E139.top"),sQuery(id+"F20.wireOp",EDGE,"E139.left")])]});
            var Q5;
            Q5=makeQuery(id+"F21.opExtrude","SWEPT_EDGE",EDGE,{"disambiguationData":[OSD([sQuery(id+"F20.wireOp",EDGE,"E139.bottom"),sQuery(id+"F20.wireOp",EDGE,"E139.right")])]});
            var Q6;
            Q6=makeQuery(id+"F21.opExtrude","SWEPT_EDGE",EDGE,{"disambiguationData":[OSD([sQuery(id+"F20.wireOp",EDGE,"E140.top"),sQuery(id+"F20.wireOp",EDGE,"E140.right")])]});
            var Q7;
            Q7=makeQuery(id+"F21.opExtrude","SWEPT_EDGE",EDGE,{"disambiguationData":[OSD([sQuery(id+"F20.wireOp",EDGE,"E139.bottom"),sQuery(id+"F20.wireOp",EDGE,"E140.bottom"),sQuery(id+"F20.wireOp",EDGE,"E140.right")])]});
            fillet(context, id + "F22", {"entities" : qUnion([Q0, Q1, Q2, Q3, Q4, Q5, Q6, Q7]), "radius" : 5 * mm, "tangentPropagation" : true, "allowEdgeOverflow" : false});
        }
    });
